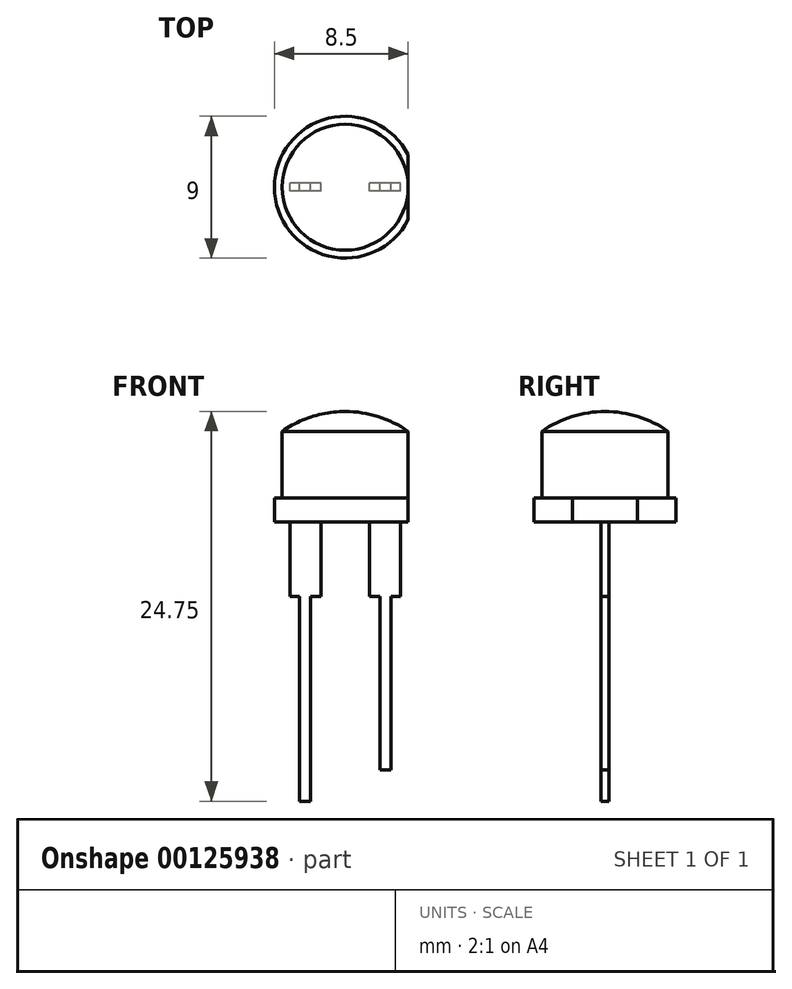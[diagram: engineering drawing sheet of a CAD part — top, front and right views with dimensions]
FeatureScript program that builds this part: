
annotation { "Feature Type Name" : "Feature", "Feature Type Description" : "" }
export const myFeature = defineFeature(function(context is Context, id is Id, definition is map)
    precondition{}
    {
        {
            var Q0;
            Q0=qCreatedBy(makeId("Front.planeOp"),FACE);
            var sketch = newSketch(context, id + "F0", { "sketchPlane" : qUnion([Q0])});
            skLineSegment(sketch, "E0", {"start": v(0, 0) * mm, "end": v(-4.5, 0) * mm});
            skLineSegment(sketch, "E1", {"start": v(-4.5, 0) * mm, "end": v(-4.5, 1.5) * mm});
            skLineSegment(sketch, "E2", {"start": v(-4.5, 1.5) * mm, "end": v(-4, 1.5) * mm});
            skLineSegment(sketch, "E3", {"start": v(-4, 1.5) * mm, "end": v(-4, 5.74) * mm});
            skLineSegment(sketch, "E4", {"start": v(0, 0) * mm, "end": v(0, 7) * mm});
            skArc(sketch, "E5", {"start": v(0, 7) * mm, "mid": v(-2.1, 6.68) * mm, "end": v(-4, 5.74) * mm});
            skSolve(sketch);
        }
        {
            var Q0;
            Q0 = qSketchRegion(id + "F0", true);
            var Q1;
            Q1=sQuery(id+"F0.wireOp",EDGE,"E4");
            revolve(context, id + "F1", {"entities" : qUnion([Q0]), "axis" : qUnion([Q1]), "revolveType" : RevolveType.FULL});
        }
        {
            var Q0;
            Q0=makeQuery(id+"F1.opRevolve","SWEPT_FACE",FACE,{"disambiguationData":[OSD([sQuery(id+"F0.wireOp",EDGE,"E0")])]});
            var sketch = newSketch(context, id + "F2", { "sketchPlane" : qUnion([Q0])});
            skLineSegment(sketch, "E6", {"start": v(4, 2.06) * mm, "end": v(4, -2.06) * mm});
            skArc(sketch, "E7", {"start": v(4, -2.06) * mm, "mid": v(4.5, 0) * mm, "end": v(4, 2.06) * mm});
            skSolve(sketch);
        }
        {
            var Q0;
            Q0 = qSketchRegion(id + "F2", true);
            extrude(context, id + "F3", {"entities" : qUnion([Q0]), "operationType" : NewBodyOperationType.REMOVE, "endBound" : BoundingType.THROUGH_ALL, "oppositeDirection" : true, "depth" : 25 * mm});
        }
        {
            var Q0;
            Q0=makeQuery(id+"F1.opRevolve","SWEPT_FACE",FACE,{"disambiguationData":[OSD([sQuery(id+"F0.wireOp",EDGE,"E0")])]});
            var sketch = newSketch(context, id + "F4", { "sketchPlane" : qUnion([Q0])});
            skLineSegment(sketch, "E8.bottom", {"start": v(3.5, 0.25) * mm, "end": v(1.55, 0.25) * mm});
            skLineSegment(sketch, "E8.top", {"start": v(3.5, -0.25) * mm, "end": v(1.55, -0.25) * mm});
            skLineSegment(sketch, "E8.left", {"start": v(3.5, 0.25) * mm, "end": v(3.5, -0.25) * mm});
            skLineSegment(sketch, "E8.right", {"start": v(1.55, 0.25) * mm, "end": v(1.55, -0.25) * mm});
            skLineSegment(sketch, "E9.left", {"start": v(-1.55, 0.25) * mm, "end": v(-1.55, -0.25) * mm});
            skLineSegment(sketch, "E9.right", {"start": v(-3.5, 0.25) * mm, "end": v(-3.5, -0.25) * mm});
            skLineSegment(sketch, "E10", {"start": v(-1.55, 0.25) * mm, "end": v(-3.5, 0.25) * mm});
            skLineSegment(sketch, "E11", {"start": v(-1.55, -0.25) * mm, "end": v(-3.5, -0.25) * mm});
            skSolve(sketch);
        }
        {
            var Q0;
            Q0 = qSketchRegion(id + "F4", true);
            extrude(context, id + "F5", {"entities" : qUnion([Q0]), "operationType" : NewBodyOperationType.ADD, "depth" : 4.75 * mm});
        }
        {
            var Q0;
            Q0=makeQuery(id+"F5.opExtrude","CAP_FACE",FACE,{"disambiguationData":[OSD([sQuery(id+"F4.wireOp",EDGE,"E8.bottom"),sQuery(id+"F4.wireOp",EDGE,"E8.top"),sQuery(id+"F4.wireOp",EDGE,"E8.left"),sQuery(id+"F4.wireOp",EDGE,"E8.right")])],"isStart":false});
            var sketch = newSketch(context, id + "F6", { "sketchPlane" : qUnion([Q0])});
            skLineSegment(sketch, "E12.bottom", {"start": v(2.9, 0.25) * mm, "end": v(2.2, 0.25) * mm});
            skLineSegment(sketch, "E12.top", {"start": v(2.9, -0.25) * mm, "end": v(2.2, -0.25) * mm});
            skLineSegment(sketch, "E12.left", {"start": v(2.9, 0.25) * mm, "end": v(2.9, -0.25) * mm});
            skLineSegment(sketch, "E12.right", {"start": v(2.2, 0.25) * mm, "end": v(2.2, -0.25) * mm});
            skSolve(sketch);
        }
        {
            var Q0;
            Q0=makeQuery(id+"F6.imprint","IMPRINT",FACE,{"disambiguationData":[TD([[makeQuery(id+"F6.imprint","IMPRINT",EDGE,{"derivedFrom":sQuery(id+"F6.wireOp",EDGE,"E12.bottom")}),1.0]])]});
            extrude(context, id + "F7", {"entities" : qUnion([Q0]), "operationType" : NewBodyOperationType.ADD, "depth" : 11 * mm});
        }
        {
            var Q0;
            Q0=makeQuery(id+"F5.opExtrude","CAP_FACE",FACE,{"disambiguationData":[OSD([sQuery(id+"F4.wireOp",EDGE,"E9.left"),sQuery(id+"F4.wireOp",EDGE,"E9.right"),sQuery(id+"F4.wireOp",EDGE,"E10"),sQuery(id+"F4.wireOp",EDGE,"E11")])],"isStart":false});
            var sketch = newSketch(context, id + "F8", { "sketchPlane" : qUnion([Q0])});
            skLineSegment(sketch, "E13.bottom", {"start": v(-2.2, 0.25) * mm, "end": v(-2.9, 0.25) * mm});
            skLineSegment(sketch, "E13.top", {"start": v(-2.2, -0.25) * mm, "end": v(-2.9, -0.25) * mm});
            skLineSegment(sketch, "E13.left", {"start": v(-2.2, 0.25) * mm, "end": v(-2.2, -0.25) * mm});
            skLineSegment(sketch, "E13.right", {"start": v(-2.9, 0.25) * mm, "end": v(-2.9, -0.25) * mm});
            skSolve(sketch);
        }
        {
            var Q0;
            Q0 = qSketchRegion(id + "F8", true);
            extrude(context, id + "F9", {"entities" : qUnion([Q0]), "operationType" : NewBodyOperationType.ADD, "depth" : 13 * mm});
        }
        {
            var Q0;
            Q0=makeQuery(id+"F1.opRevolve","SWEPT_BODY",BODY,{"disambiguationData":[OSD([sQuery(id+"F0.wireOp",EDGE,"E0"),sQuery(id+"F0.wireOp",EDGE,"E1"),sQuery(id+"F0.wireOp",EDGE,"E2"),sQuery(id+"F0.wireOp",EDGE,"E3"),sQuery(id+"F0.wireOp",EDGE,"E4"),sQuery(id+"F0.wireOp",EDGE,"E5")])]});
            transform(context, id + "F10", {"entities" : qUnion([Q0]), "transformType" : TransformType.TRANSLATION_3D, "dx" : 0 * mm, "dy" : 0 * mm, "dz" : 0 * mm, "makeCopy" : true});
        }
        {
            var Q0;
            Q0=makeQuery(id+"F10.opPattern","COPY",BODY,{"derivedFrom":makeQuery(id+"F1.opRevolve","SWEPT_BODY",BODY,{"disambiguationData":[OSD([sQuery(id+"F0.wireOp",EDGE,"E0"),sQuery(id+"F0.wireOp",EDGE,"E1"),sQuery(id+"F0.wireOp",EDGE,"E2"),sQuery(id+"F0.wireOp",EDGE,"E3"),sQuery(id+"F0.wireOp",EDGE,"E4"),sQuery(id+"F0.wireOp",EDGE,"E5")])]}),"instanceName":"1"});
            deleteBodies(context, id + "F11", {"entities" : qUnion([Q0])});
        }
    });
